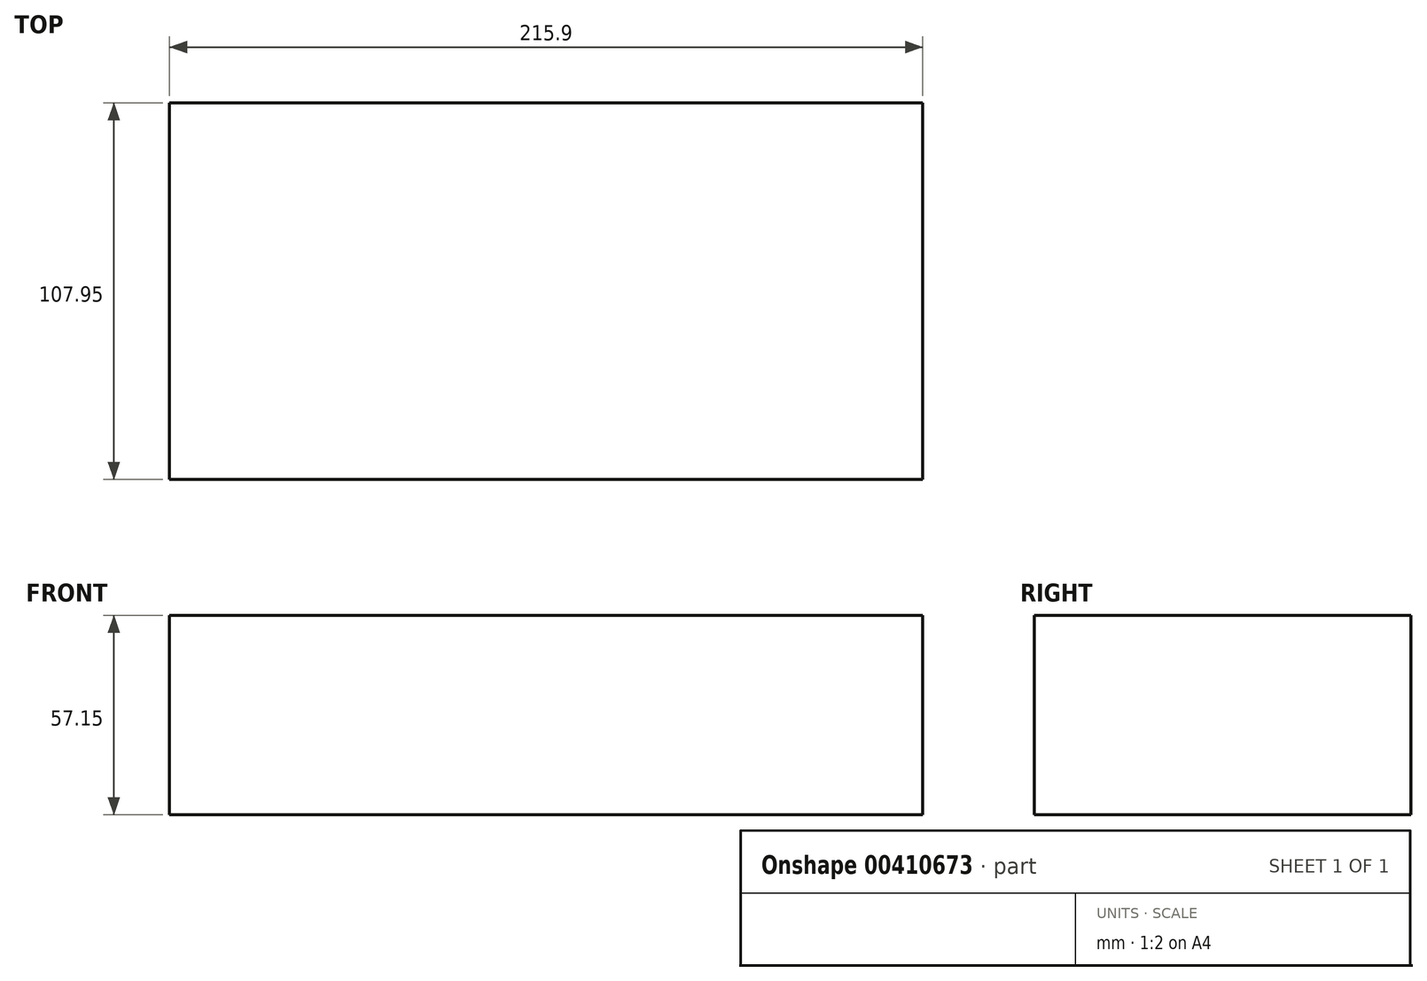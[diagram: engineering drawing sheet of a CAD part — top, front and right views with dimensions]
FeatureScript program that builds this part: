
annotation { "Feature Type Name" : "Feature", "Feature Type Description" : "" }
export const myFeature = defineFeature(function(context is Context, id is Id, definition is map)
    precondition{}
    {
        {
            var Q0;
            Q0=qCreatedBy(makeId("Top.planeOp"),FACE);
            var sketch = newSketch(context, id + "F0", { "sketchPlane" : qUnion([Q0])});
            skLineSegment(sketch, "E0.bottom", {"start": v(-182.95, 86.62) * mm, "end": v(32.95, 86.62) * mm});
            skLineSegment(sketch, "E0.top", {"start": v(-182.95, -21.33) * mm, "end": v(32.95, -21.33) * mm});
            skLineSegment(sketch, "E0.left", {"start": v(-182.95, 86.62) * mm, "end": v(-182.95, -21.33) * mm});
            skLineSegment(sketch, "E0.right", {"start": v(32.95, 86.62) * mm, "end": v(32.95, -21.33) * mm});
            skSolve(sketch);
        }
        {
            var Q0;
            Q0=makeQuery(id+"F0.imprint","IMPRINT",FACE,{"disambiguationData":[TD([[makeQuery(id+"F0.imprint","IMPRINT",EDGE,{"derivedFrom":sQuery(id+"F0.wireOp",EDGE,"E0.bottom")}),-1.0]])]});
            extrude(context, id + "F1", {"entities" : qUnion([Q0]), "depth" : 57.15 * mm});
        }
    });
